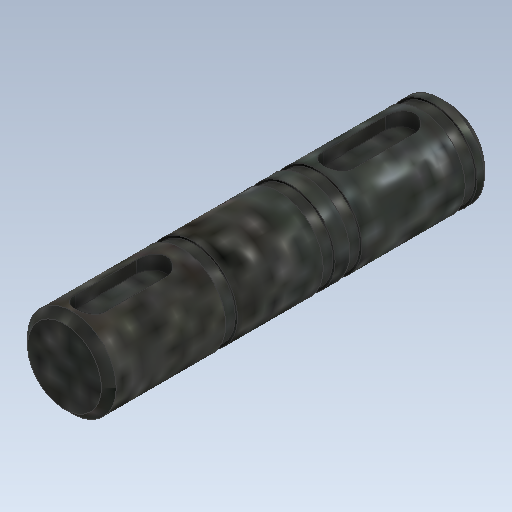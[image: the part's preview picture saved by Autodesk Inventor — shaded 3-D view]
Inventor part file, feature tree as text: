
AUTODESK INVENTOR PART (.ipt)
format: ipt  version: 2021 (Build 250183000, 183)  size: 331,776 bytes
history: native  units: mm
features: revolve x2, plane x1, extrude x1, chamfer x1, sketch x1, projected_geometry x1
ambient origin geometry x8: Origin, YZ Plane, XZ Plane, XY Plane, X Axis, Y Axis, Z Axis, Center Point
bodies: Solid1 (feature_tree)
feature tree (7):
  revolve  "Revolution1"  [1 undecoded]
  revolve  "Revolution2"  Angle=90.0deg
  plane  "Work Plane2"
  extrude  "Extrusion2"  TaperAngle=90.0deg  [1 undecoded]
  chamfer  "Chamfer3"  Distance=2.85mm
  sketch  "Sketch1"  dims[d0=3.0mm d1=25.9mm d2=90.0deg d4=90.0deg d33=2.85mm d34=0.8mm d35=2.85mm d49=6.15mm d50=1.0mm d52=1.0mm d53=0.0mm d54=0.5mm d55=2.0mm d56=45.0deg d57=5.8mm d58=7.0mm d59=1.0mm d60=3.5mm d61=3.5mm d63=1.0mm d64=6.15mm d65=1.0mm d66=1.75mm]
  projected_geometry  "Projected Loop4"
note: 2 required parameter values undecoded (feature->parameter linkage not recoverable at this tier; creation-order binding heuristic only, values carry confidence <= 0.55)